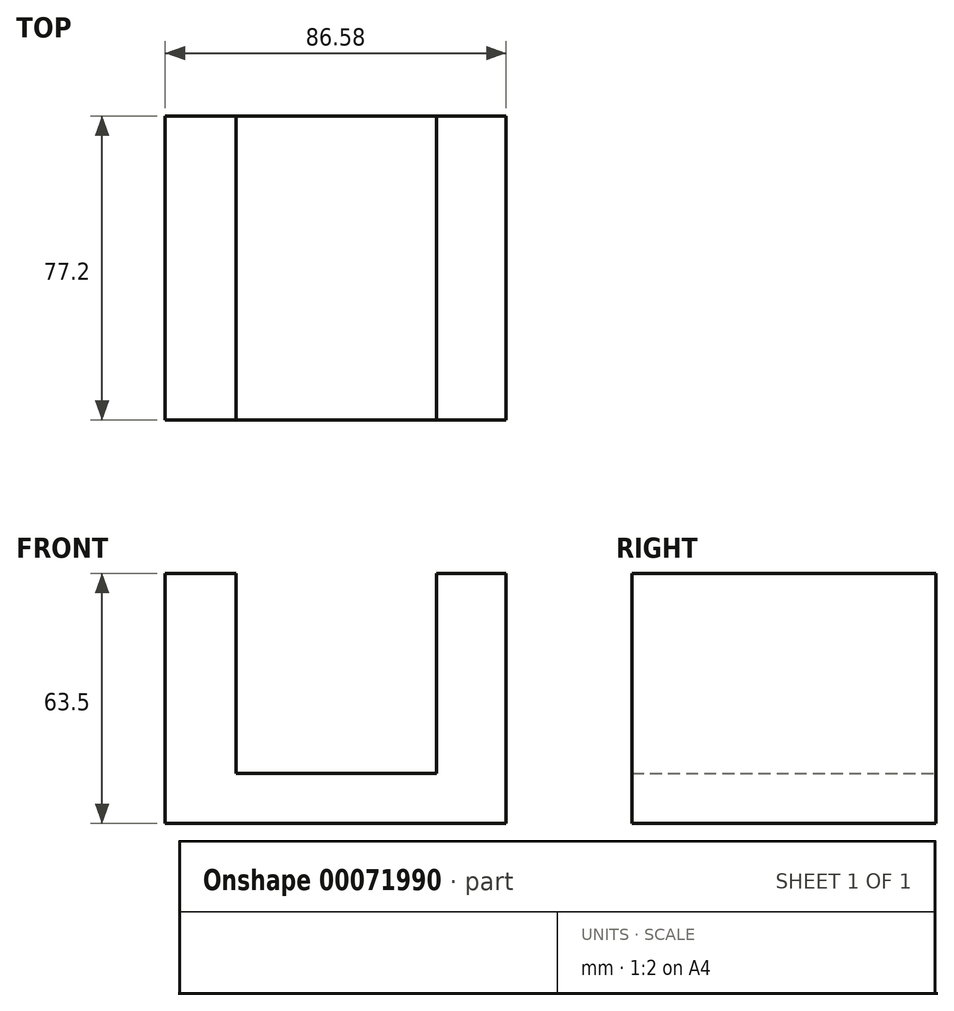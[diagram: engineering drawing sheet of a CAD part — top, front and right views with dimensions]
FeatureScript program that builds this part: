
annotation { "Feature Type Name" : "Feature", "Feature Type Description" : "" }
export const myFeature = defineFeature(function(context is Context, id is Id, definition is map)
    precondition{}
    {
        {
            var Q0;
            Q0=qCreatedBy(makeId("Top.planeOp"),FACE);
            var sketch = newSketch(context, id + "F0", { "sketchPlane" : qUnion([Q0])});
            skLineSegment(sketch, "E0.bottom", {"start": v(0, 0) * mm, "end": v(86.58, 0) * mm});
            skLineSegment(sketch, "E0.top", {"start": v(0, 77.2) * mm, "end": v(86.58, 77.2) * mm});
            skLineSegment(sketch, "E0.left", {"start": v(0, 0) * mm, "end": v(0, 77.2) * mm});
            skLineSegment(sketch, "E0.right", {"start": v(86.58, 0) * mm, "end": v(86.58, 77.2) * mm});
            skSolve(sketch);
        }
        {
            var Q0;
            Q0=makeQuery(id+"F0.imprint","IMPRINT",FACE,{"disambiguationData":[TD([[makeQuery(id+"F0.imprint","IMPRINT",EDGE,{"derivedFrom":sQuery(id+"F0.wireOp",EDGE,"E0.bottom")}),1.0]])]});
            extrude(context, id + "F1", {"entities" : qUnion([Q0]), "depth" : 12.7 * mm});
        }
        {
            var Q0;
            Q0=makeQuery(id+"F1.opExtrude","CAP_FACE",FACE,{"disambiguationData":[OSD([sQuery(id+"F0.wireOp",EDGE,"E0.bottom"),sQuery(id+"F0.wireOp",EDGE,"E0.top"),sQuery(id+"F0.wireOp",EDGE,"E0.left"),sQuery(id+"F0.wireOp",EDGE,"E0.right")])],"isStart":false});
            var sketch = newSketch(context, id + "F2", { "sketchPlane" : qUnion([Q0])});
            skLineSegment(sketch, "E1.bottom", {"start": v(0, 0) * mm, "end": v(18.03, 0) * mm});
            skLineSegment(sketch, "E1.top", {"start": v(0, 77.2) * mm, "end": v(18.03, 77.2) * mm});
            skLineSegment(sketch, "E1.left", {"start": v(0, 0) * mm, "end": v(0, 77.2) * mm});
            skLineSegment(sketch, "E1.right", {"start": v(18.03, 0) * mm, "end": v(18.03, 77.2) * mm});
            skLineSegment(sketch, "E2.bottom", {"start": v(86.58, 0) * mm, "end": v(68.89, 0) * mm});
            skLineSegment(sketch, "E2.top", {"start": v(86.58, 77.2) * mm, "end": v(68.89, 77.2) * mm});
            skLineSegment(sketch, "E2.left", {"start": v(86.58, 0) * mm, "end": v(86.58, 77.2) * mm});
            skLineSegment(sketch, "E2.right", {"start": v(68.89, 0) * mm, "end": v(68.89, 77.2) * mm});
            skSolve(sketch);
        }
        {
            var Q0;
            Q0=makeQuery(id+"F2.imprint","IMPRINT",FACE,{"disambiguationData":[TD([[makeQuery(id+"F2.imprint","IMPRINT",EDGE,{"derivedFrom":sQuery(id+"F2.wireOp",EDGE,"E2.bottom")}),1.0]])]});
            var Q1;
            Q1=makeQuery(id+"F2.imprint","IMPRINT",FACE,{"disambiguationData":[TD([[makeQuery(id+"F2.imprint","IMPRINT",EDGE,{"derivedFrom":sQuery(id+"F2.wireOp",EDGE,"E1.bottom")}),1.0]])]});
            extrude(context, id + "F3", {"entities" : qUnion([Q0, Q1]), "operationType" : NewBodyOperationType.ADD, "depth" : 50.8 * mm});
        }
    });
